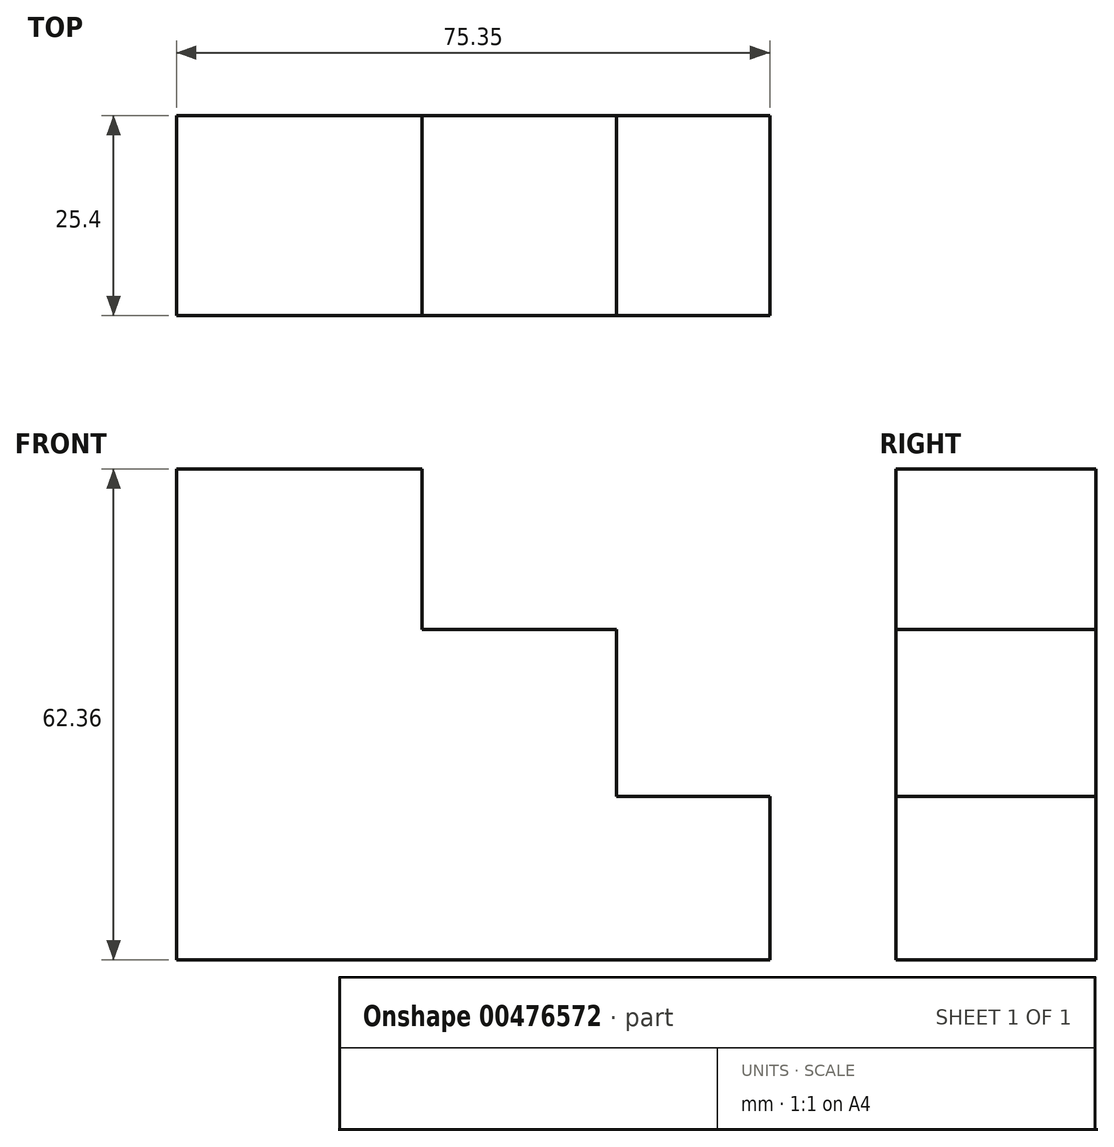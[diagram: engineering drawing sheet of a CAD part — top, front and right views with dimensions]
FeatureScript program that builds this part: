
annotation { "Feature Type Name" : "Feature", "Feature Type Description" : "" }
export const myFeature = defineFeature(function(context is Context, id is Id, definition is map)
    precondition{}
    {
        {
            var Q0;
            Q0=qCreatedBy(makeId("Front.planeOp"),FACE);
            var sketch = newSketch(context, id + "F0", { "sketchPlane" : qUnion([Q0])});
            skLineSegment(sketch, "E0", {"start": v(0, 0) * mm, "end": v(75.35, 0) * mm});
            skLineSegment(sketch, "E1", {"start": v(75.35, 0) * mm, "end": v(75.35, 20.79) * mm});
            skLineSegment(sketch, "E2", {"start": v(75.35, 20.79) * mm, "end": v(55.87, 20.79) * mm});
            skLineSegment(sketch, "E3", {"start": v(55.87, 20.79) * mm, "end": v(55.87, 42) * mm});
            skLineSegment(sketch, "E4", {"start": v(55.87, 42) * mm, "end": v(31.18, 42) * mm});
            skLineSegment(sketch, "E5", {"start": v(31.18, 42) * mm, "end": v(31.18, 62.36) * mm});
            skLineSegment(sketch, "E6", {"start": v(31.18, 62.36) * mm, "end": v(0, 62.36) * mm});
            skLineSegment(sketch, "E7", {"start": v(0, 62.36) * mm, "end": v(0, 0) * mm});
            skSolve(sketch);
        }
        {
            var Q0;
            Q0=makeQuery(id+"F0.imprint","IMPRINT",FACE,{"disambiguationData":[TD([[makeQuery(id+"F0.imprint","IMPRINT",EDGE,{"derivedFrom":sQuery(id+"F0.wireOp",EDGE,"E0")}),1.0]])]});
            extrude(context, id + "F1", {"entities" : qUnion([Q0]), "depth" : 25.4 * mm});
        }
    });
